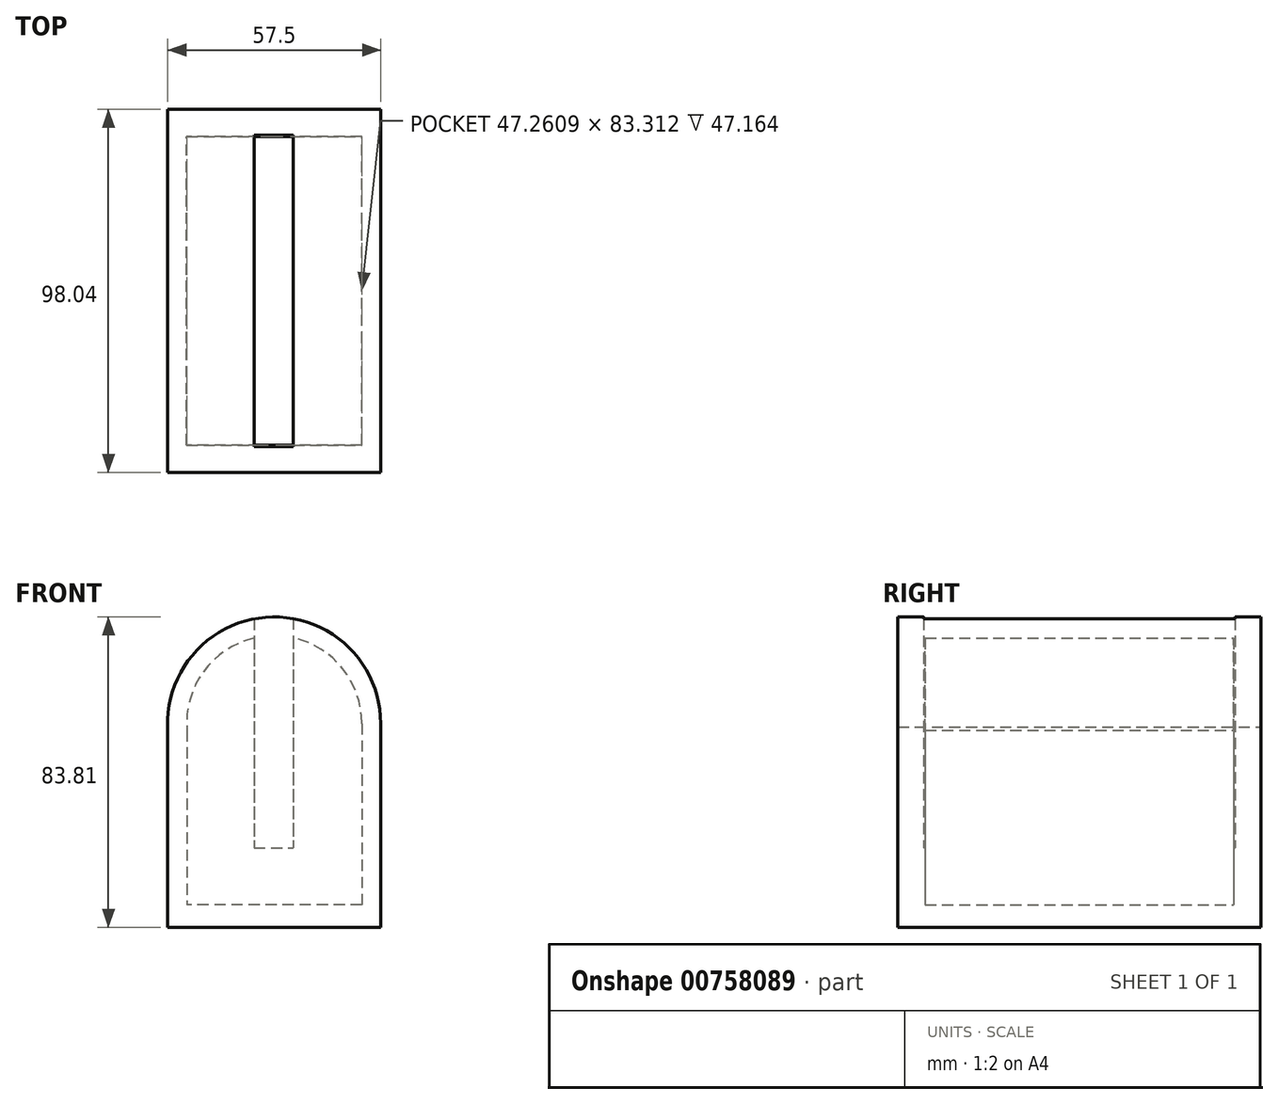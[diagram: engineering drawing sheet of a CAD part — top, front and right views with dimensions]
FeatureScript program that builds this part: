
annotation { "Feature Type Name" : "Feature", "Feature Type Description" : "" }
export const myFeature = defineFeature(function(context is Context, id is Id, definition is map)
    precondition{}
    {
        {
            var Q0;
            Q0=qCreatedBy(makeId("Front.planeOp"),FACE);
            var sketch = newSketch(context, id + "F0", { "sketchPlane" : qUnion([Q0])});
            skCircle(sketch, "E0", {"center": v(0, 33.58) * mm, "radius": 28.75 * mm});
            skLineSegment(sketch, "E1.bottom", {"start": v(28.75, 33.58) * mm, "end": v(-28.74, 33.58) * mm});
            skLineSegment(sketch, "E1.top", {"start": v(28.75, -21.48) * mm, "end": v(-28.74, -21.48) * mm});
            skLineSegment(sketch, "E1.left", {"start": v(28.75, 33.58) * mm, "end": v(28.75, -21.48) * mm});
            skLineSegment(sketch, "E1.right", {"start": v(-28.74, 33.58) * mm, "end": v(-28.74, -21.48) * mm});
            skSolve(sketch);
        }
        {
            var Q0;
            {var subQ0=sQuery(id+"F0.wireOp",EDGE,"E1.bottom");Q0=makeQuery(id+"F0.imprint","IMPRINT",FACE,{"disambiguationData":[TD([[makeQuery(id+"F0.imprint","IMPRINT",EDGE,{"derivedFrom":subQ0}),-1.0]])]});}
            var Q1;
            {var subQ0=sQuery(id+"F0.wireOp",EDGE,"E1.bottom");Q1=makeQuery(id+"F0.imprint","IMPRINT",FACE,{"disambiguationData":[TD([[makeQuery(id+"F0.imprint","IMPRINT",EDGE,{"derivedFrom":subQ0}),1.0]])]});}
            var Q2;
            {var subQ4=sQuery(id+"F0.wireOp",EDGE,"E1.top");Q2=makeQuery(id+"F0.imprint","IMPRINT",FACE,{"disambiguationData":[TD([[makeQuery(id+"F0.imprint","IMPRINT",EDGE,{"derivedFrom":subQ4}),-1.0]])]});}
            extrude(context, id + "F1", {"entities" : qUnion([Q0, Q1, Q2]), "depth" : 49.02 * mm, "offsetDistance" : 25.4 * mm});
        }
        {
            var Q0;
            Q0=makeQuery(id+"F1.opExtrude","CAP_FACE",FACE,{"disambiguationData":[OSD([sQuery(id+"F0.wireOp",EDGE,"E0"),sQuery(id+"F0.wireOp",EDGE,"E1.top"),sQuery(id+"F0.wireOp",EDGE,"E1.left"),sQuery(id+"F0.wireOp",EDGE,"E1.right")])],"isStart":true});
            var sketch = newSketch(context, id + "F2", { "sketchPlane" : qUnion([Q0])});
            skCircle(sketch, "E2", {"center": v(0, 33.58) * mm, "radius": 23.67 * mm});
            skLineSegment(sketch, "E3.bottom", {"start": v(-23.67, 33.58) * mm, "end": v(23.6, 33.58) * mm});
            skLineSegment(sketch, "E3.top", {"start": v(-23.67, -15.43) * mm, "end": v(23.6, -15.43) * mm});
            skLineSegment(sketch, "E3.left", {"start": v(-23.67, 33.58) * mm, "end": v(-23.67, -15.43) * mm});
            skLineSegment(sketch, "E3.right", {"start": v(23.6, 33.58) * mm, "end": v(23.6, -15.43) * mm});
            skSolve(sketch);
        }
        {
            var Q0;
            {var subQ0=sQuery(id+"F2.wireOp",EDGE,"E3.bottom");Q0=makeQuery(id+"F2.imprint","IMPRINT",FACE,{"disambiguationData":[TD([[makeQuery(id+"F2.imprint","IMPRINT",EDGE,{"derivedFrom":subQ0}),1.0]])]});}
            var Q1;
            {var subQ0=sQuery(id+"F2.wireOp",EDGE,"E3.bottom");Q1=makeQuery(id+"F2.imprint","IMPRINT",FACE,{"disambiguationData":[TD([[makeQuery(id+"F2.imprint","IMPRINT",EDGE,{"derivedFrom":subQ0}),-1.0]])]});}
            var Q2;
            {var subQ4=sQuery(id+"F2.wireOp",EDGE,"E3.top");Q2=makeQuery(id+"F2.imprint","IMPRINT",FACE,{"disambiguationData":[TD([[makeQuery(id+"F2.imprint","IMPRINT",EDGE,{"derivedFrom":subQ4}),1.0]])]});}
            extrude(context, id + "F3", {"entities" : qUnion([Q0, Q1, Q2]), "operationType" : NewBodyOperationType.REMOVE, "oppositeDirection" : true, "depth" : 41.66 * mm, "offsetDistance" : 25.4 * mm});
        }
        {
            var Q0;
            Q0=qCreatedBy(makeId("Top.planeOp"),FACE);
            var sketch = newSketch(context, id + "F4", { "sketchPlane" : qUnion([Q0])});
            skLineSegment(sketch, "E4.bottom", {"start": v(-5.44, 0) * mm, "end": v(5.14, 0) * mm});
            skLineSegment(sketch, "E4.top", {"start": v(-5.44, -42.05) * mm, "end": v(5.14, -42.05) * mm});
            skLineSegment(sketch, "E4.left", {"start": v(-5.44, 0) * mm, "end": v(-5.44, -42.05) * mm});
            skLineSegment(sketch, "E4.right", {"start": v(5.14, 0) * mm, "end": v(5.14, -42.05) * mm});
            skSolve(sketch);
        }
        {
            var Q0;
            Q0=makeQuery(id+"F4.imprint","IMPRINT",FACE,{"disambiguationData":[TD([[makeQuery(id+"F4.imprint","IMPRINT",EDGE,{"derivedFrom":sQuery(id+"F4.wireOp",EDGE,"E4.bottom")}),-1.0]])]});
            extrude(context, id + "F5", {"entities" : qUnion([Q0]), "operationType" : NewBodyOperationType.REMOVE, "depth" : 108.7 * mm, "offsetDistance" : 25.4 * mm});
        }
        {
            var Q0;
            Q0=makeQuery(id+"F1.opExtrude","SWEPT_BODY",BODY,{"disambiguationData":[OSD([sQuery(id+"F0.wireOp",EDGE,"E0"),sQuery(id+"F0.wireOp",EDGE,"E1.top"),sQuery(id+"F0.wireOp",EDGE,"E1.left"),sQuery(id+"F0.wireOp",EDGE,"E1.right")])]});
            var Q1;
            Q1=qCreatedBy(makeId("Front.planeOp"),FACE);
            mirror(context, id + "F6", {"operationType" : NewBodyOperationType.ADD, "entities" : qUnion([Q0]), "mirrorPlane" : qUnion([Q1])});
        }
    });
